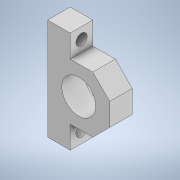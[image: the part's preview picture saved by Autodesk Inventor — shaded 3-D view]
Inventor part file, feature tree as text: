
AUTODESK INVENTOR PART (.ipt)
format: ipt  version: 2022 (Build 260153000, 153)  size: 131,584 bytes
history: native  units: mm
features: extrude x3, sketch x3, other x1
ambient origin geometry x8: Origin, YZ Plane, XZ Plane, XY Plane, X Axis, Y Axis, Z Axis, Center Point
bodies: Body1 (feature_tree)
feature tree (7):
  other  "Sólido1"
  extrude  "Extrusión1"  Depth=20.0mm TaperAngle=0.0deg
  extrude  "Extrusión2"  Depth=20.0mm TaperAngle=0.0deg
  extrude  "Extrusión3"  Depth=20.0mm TaperAngle=0.0deg
  sketch  "Boceto1"  dims[d0=20.0mm d1=20.0mm d2=20.0mm d3=90.0mm d4=20.0mm d5=20.0mm d6=55.0mm d7=30.0mm d8=20.0mm d9=0.0mm]
  sketch  "Boceto2"  dims[d11=10.0mm d12=20.0mm d13=0.0mm]
  sketch  "Boceto3"  dims[d14=10.0mm d15=20.0mm d16=0.0mm]
